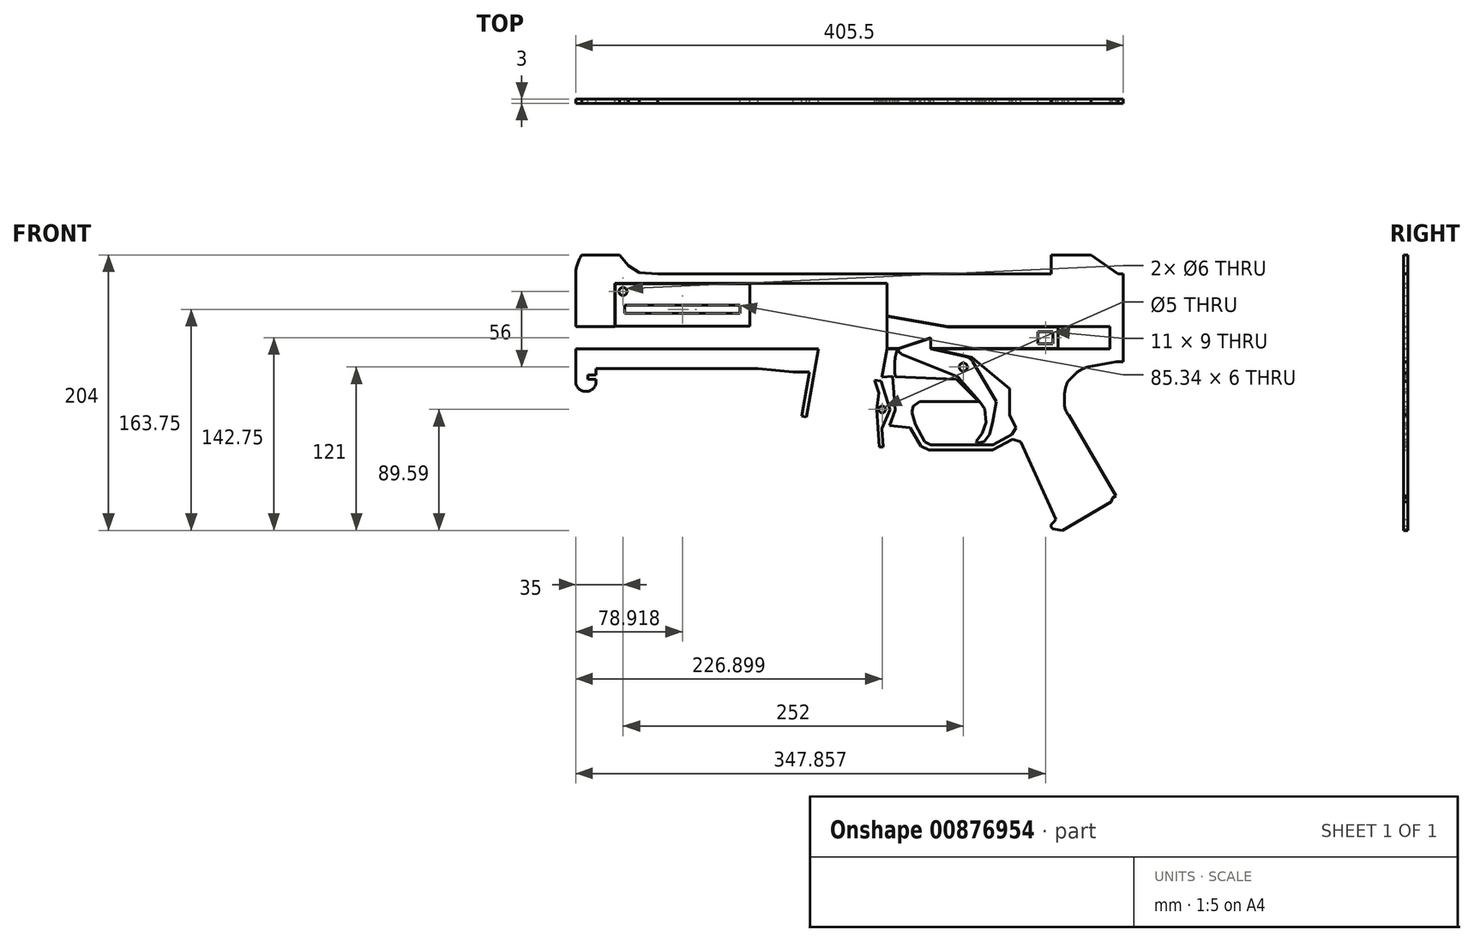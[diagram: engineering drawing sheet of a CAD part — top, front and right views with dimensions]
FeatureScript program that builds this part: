
annotation { "Feature Type Name" : "Feature", "Feature Type Description" : "" }
export const myFeature = defineFeature(function(context is Context, id is Id, definition is map)
    precondition{}
    {
        {
            var Q0;
            Q0=qCreatedBy(makeId("Front.planeOp"),FACE);
            var sketch = newSketch(context, id + "F0", { "sketchPlane" : qUnion([Q0])});
            skLineSegment(sketch, "E0", {"start": v(53.5, -65) * mm, "end": v(53.5, 0) * mm});
            skLineSegment(sketch, "E1", {"start": v(0, 0) * mm, "end": v(0, 14) * mm});
            skLineSegment(sketch, "E2", {"start": v(0, 14) * mm, "end": v(29.55, 14) * mm});
            skPoint(sketch, "E3.visualSharp", {"position": v(0, 14) * mm});
            skPoint(sketch, "E4.visualSharp", {"position": v(29.55, 14) * mm});
            skPoint(sketch, "E5.visualSharp", {"position": v(53.5, 0) * mm});
            skPoint(sketch, "E6.visualSharp", {"position": v(0, 0) * mm});
            skLineSegment(sketch, "E7", {"start": v(53.5, -65) * mm, "end": v(48.5, -65) * mm});
            skLineSegment(sketch, "E8", {"start": v(48.5, -65) * mm, "end": v(27.5, -69) * mm});
            skLineSegment(sketch, "E9", {"start": v(18.5, -73.5) * mm, "end": v(12.5, -79.5) * mm});
            skLineSegment(sketch, "E10", {"start": v(10, -90.5) * mm, "end": v(10, -96.5) * mm});
            skLineSegment(sketch, "E11", {"start": v(13, -104.5) * mm, "end": v(48, -164.5) * mm});
            skLineSegment(sketch, "E12", {"start": v(48, -164.5) * mm, "end": v(45.5, -166) * mm});
            skLineSegment(sketch, "E13", {"start": v(45.5, -166) * mm, "end": v(44.5, -169) * mm});
            skLineSegment(sketch, "E14", {"start": v(44.5, -169) * mm, "end": v(8.5, -190) * mm});
            skLineSegment(sketch, "E15", {"start": v(8.5, -190) * mm, "end": v(1.5, -189) * mm});
            skLineSegment(sketch, "E16", {"start": v(1.5, -189) * mm, "end": v(-0.5, -186.5) * mm});
            skLineSegment(sketch, "E17", {"start": v(-0.5, -186.5) * mm, "end": v(3.5, -182) * mm});
            skLineSegment(sketch, "E18", {"start": v(3.5, -182) * mm, "end": v(-22.5, -124.5) * mm});
            skLineSegment(sketch, "E19", {"start": v(-22.5, -124.5) * mm, "end": v(-28.5, -122.5) * mm});
            skLineSegment(sketch, "E20", {"start": v(-28.5, -122.5) * mm, "end": v(-43.5, -130.5) * mm});
            skLineSegment(sketch, "E21", {"start": v(-43.5, -130.5) * mm, "end": v(-90.5, -130.5) * mm});
            skLineSegment(sketch, "E22", {"start": v(-90.5, -130.5) * mm, "end": v(-96.5, -127.5) * mm});
            skLineSegment(sketch, "E23", {"start": v(-96.5, -127.5) * mm, "end": v(-104.5, -114) * mm});
            skLineSegment(sketch, "E24", {"start": v(-104.5, -114) * mm, "end": v(-131.43, -111) * mm, "construction": true});
            skArc(sketch, "E25", {"start": v(10, -90.5) * mm, "mid": v(10.63, -84.86) * mm, "end": v(12.5, -79.5) * mm});
            skArc(sketch, "E26", {"start": v(27.5, -69) * mm, "mid": v(22.69, -70.63) * mm, "end": v(18.5, -73.5) * mm});
            skArc(sketch, "E27", {"start": v(10, -96.5) * mm, "mid": v(10.77, -100.77) * mm, "end": v(13, -104.5) * mm});
            skLineSegment(sketch, "E28", {"start": v(0, 0) * mm, "end": v(-291.5, 0) * mm});
            skLineSegment(sketch, "E29", {"start": v(-291.5, 0) * mm, "end": v(-305, 1) * mm});
            skLineSegment(sketch, "E30", {"start": v(-319.5, 14) * mm, "end": v(-347.5, 14) * mm});
            skLineSegment(sketch, "E31", {"start": v(-345, -87) * mm, "end": v(-344, -87) * mm});
            skLineSegment(sketch, "E32", {"start": v(-337, -70) * mm, "end": v(-217, -70) * mm});
            skLineSegment(sketch, "E33", {"start": v(-217, -70) * mm, "end": v(-191, -72.5) * mm});
            skLineSegment(sketch, "E34", {"start": v(-191, -72.5) * mm, "end": v(-179, -72.5) * mm});
            skLineSegment(sketch, "E35", {"start": v(-179, -72.5) * mm, "end": v(-184.82, -105.5) * mm});
            skArc(sketch, "E36", {"start": v(-352, 0) * mm, "mid": v(-350.85, 7.35) * mm, "end": v(-347.5, 14) * mm});
            skLineSegment(sketch, "E37", {"start": v(-305, 1) * mm, "end": v(-313, 6) * mm});
            skLineSegment(sketch, "E38", {"start": v(-313, 6) * mm, "end": v(-319.5, 14) * mm});
            skLineSegment(sketch, "E39.bottom", {"start": v(-323, -7) * mm, "end": v(-209, -7) * mm});
            skLineSegment(sketch, "E39.left", {"start": v(-323, -7) * mm, "end": v(-323, -39) * mm});
            skLineSegment(sketch, "E40", {"start": v(-352, -80) * mm, "end": v(-352, -55.5) * mm});
            skLineSegment(sketch, "E41", {"start": v(-352, 0) * mm, "end": v(-352, -39) * mm});
            skLineSegment(sketch, "E42", {"start": v(-352, -39) * mm, "end": v(-323, -39) * mm});
            skLineSegment(sketch, "E43", {"start": v(-30.75, -104.75) * mm, "end": v(-26, -114) * mm});
            skLineSegment(sketch, "E44", {"start": v(-26, -114) * mm, "end": v(-29, -119) * mm});
            skLineSegment(sketch, "E45", {"start": v(-29, -119) * mm, "end": v(-43, -126.5) * mm});
            skLineSegment(sketch, "E46", {"start": v(-43, -126.5) * mm, "end": v(-89, -126.5) * mm});
            skLineSegment(sketch, "E47", {"start": v(-89, -126.5) * mm, "end": v(-93.5, -124.5) * mm});
            skLineSegment(sketch, "E48", {"start": v(-93.5, -124.5) * mm, "end": v(-100.5, -111.5) * mm});
            skLineSegment(sketch, "E49", {"start": v(-100.5, -111.5) * mm, "end": v(-103, -102.5) * mm});
            skLineSegment(sketch, "E50", {"start": v(-103, -102.5) * mm, "end": v(-102, -98) * mm});
            skLineSegment(sketch, "E51", {"start": v(-102, -98) * mm, "end": v(-97.5, -94.5) * mm});
            skLineSegment(sketch, "E52", {"start": v(-55.5, -124) * mm, "end": v(-55, -125) * mm});
            skLineSegment(sketch, "E53", {"start": v(-55, -125) * mm, "end": v(-52.5, -125) * mm});
            skLineSegment(sketch, "E54", {"start": v(-52.5, -125) * mm, "end": v(-49.5, -124) * mm});
            skLineSegment(sketch, "E55", {"start": v(-49.5, -124) * mm, "end": v(-45.5, -119) * mm});
            skLineSegment(sketch, "E56", {"start": v(-45.5, -119) * mm, "end": v(-43.5, -110.5) * mm});
            skLineSegment(sketch, "E57", {"start": v(-55.5, -124) * mm, "end": v(-51, -118) * mm});
            skLineSegment(sketch, "E58", {"start": v(-51, -118) * mm, "end": v(-48, -110) * mm});
            skLineSegment(sketch, "E59", {"start": v(-48, -110) * mm, "end": v(-49, -100) * mm});
            skLineSegment(sketch, "E60", {"start": v(-49, -100) * mm, "end": v(-53, -94.5) * mm});
            skLineSegment(sketch, "E61", {"start": v(-181.32, -106) * mm, "end": v(-184.82, -105.5) * mm});
            skLineSegment(sketch, "E62", {"start": v(-181.32, -106) * mm, "end": v(-172.41, -55.5) * mm});
            skLineSegment(sketch, "E63", {"start": v(-172.41, -55.5) * mm, "end": v(-352, -55.5) * mm});
            skLineSegment(sketch, "E64", {"start": v(-131.43, -111) * mm, "end": v(-121.64, -55.5) * mm, "construction": true});
            skLineSegment(sketch, "E65", {"start": v(43.5, -55.5) * mm, "end": v(43.5, -39) * mm});
            skLineSegment(sketch, "E66", {"start": v(43.5, -39) * mm, "end": v(-76.5, -39) * mm});
            skLineSegment(sketch, "E67", {"start": v(-121.64, -55.25) * mm, "end": v(-121.64, -31.25) * mm});
            skLineSegment(sketch, "E68", {"start": v(-76.5, -39) * mm, "end": v(-121.64, -31) * mm});
            skPoint(sketch, "E69", {"position": v(-317, -13) * mm});
            skPoint(sketch, "E70", {"position": v(-215, -13) * mm});
            skLineSegment(sketch, "E71", {"start": v(5.36, -55.25) * mm, "end": v(5.36, -39.25) * mm});
            skLineSegment(sketch, "E72", {"start": v(5.36, -39.25) * mm, "end": v(-76.5, -39.25) * mm});
            skLineSegment(sketch, "E73", {"start": v(-76.5, -39.25) * mm, "end": v(-121.64, -31.25) * mm});
            skLineSegment(sketch, "E74.bottom", {"start": v(-322.75, -7.25) * mm, "end": v(-223.16, -7.25) * mm});
            skLineSegment(sketch, "E74.top", {"start": v(-322.75, -38.75) * mm, "end": v(-223.16, -38.75) * mm});
            skLineSegment(sketch, "E74.left", {"start": v(-322.75, -7.25) * mm, "end": v(-322.75, -38.75) * mm});
            skLineSegment(sketch, "E74.right", {"start": v(-223.16, -7.25) * mm, "end": v(-223.16, -38.75) * mm});
            skLineSegment(sketch, "E75", {"start": v(-209, -7) * mm, "end": v(-121.64, -7) * mm});
            skLineSegment(sketch, "E76", {"start": v(-121.64, -7) * mm, "end": v(-121.64, -31) * mm});
            skPoint(sketch, "E77", {"position": v(-65, -69) * mm});
            skLineSegment(sketch, "E78", {"start": v(-40.5, -94.5) * mm, "end": v(-58.13, -64.9) * mm});
            skLineSegment(sketch, "E79", {"start": v(5.36, -55.25) * mm, "end": v(-89, -55.25) * mm});
            skLineSegment(sketch, "E80", {"start": v(-89.25, -55.5) * mm, "end": v(-63.29, -61.19) * mm});
            skLineSegment(sketch, "E81", {"start": v(-121.64, -55.25) * mm, "end": v(-113, -55.25) * mm});
            skLineSegment(sketch, "E82", {"start": v(-89, -55.25) * mm, "end": v(-89, -47.25) * mm});
            skLineSegment(sketch, "E83", {"start": v(-89, -47.25) * mm, "end": v(-113, -55.25) * mm});
            skLineSegment(sketch, "E84", {"start": v(-89.25, -55.5) * mm, "end": v(-89.25, -47.5) * mm});
            skLineSegment(sketch, "E85", {"start": v(-89.25, -47.5) * mm, "end": v(-113.25, -55.5) * mm});
            skPoint(sketch, "E86", {"position": v(-110.25, -59.5) * mm});
            skLineSegment(sketch, "E87", {"start": v(-110.25, -59.5) * mm, "end": v(-69, -76) * mm});
            skArc(sketch, "E88", {"start": v(-110.25, -59.5) * mm, "mid": v(-112.31, -57.92) * mm, "end": v(-113.25, -55.5) * mm});
            skLineSegment(sketch, "E89", {"start": v(-97.5, -94.5) * mm, "end": v(-53.5, -94.5) * mm});
            skLineSegment(sketch, "E90", {"start": v(-70, -78) * mm, "end": v(-115.3, -76.3) * mm});
            skLineSegment(sketch, "E91", {"start": v(-53, -94.5) * mm, "end": v(-69, -76) * mm});
            skLineSegment(sketch, "E92", {"start": v(-53.5, -94.5) * mm, "end": v(-70, -78) * mm});
            skLineSegment(sketch, "E93", {"start": v(-121.64, -55.5) * mm, "end": v(-114, -55.5) * mm});
            skArc(sketch, "E94", {"start": v(-114, -55.5) * mm, "mid": v(-115.73, -65.83) * mm, "end": v(-115.3, -76.3) * mm});
            skLineSegment(sketch, "E95", {"start": v(-43.5, -110.5) * mm, "end": v(-40.5, -94.5) * mm});
            skLineSegment(sketch, "E96", {"start": v(43.5, -55.5) * mm, "end": v(-87, -55.5) * mm});
            skLineSegment(sketch, "E97", {"start": v(-87, -55.5) * mm, "end": v(-58.5, -61.74) * mm});
            skLineSegment(sketch, "E98", {"start": v(-58.5, -61.74) * mm, "end": v(-30.75, -84.92) * mm});
            skPoint(sketch, "E99.visualSharp", {"position": v(-352, -87) * mm});
            skArc(sketch, "E99.filletArc", {"start": v(-352, -80) * mm, "mid": v(-349.95, -84.95) * mm, "end": v(-345, -87) * mm});
            skPoint(sketch, "E100.visualSharp", {"position": v(-337, -87) * mm});
            skArc(sketch, "E100.filletArc", {"start": v(-344, -87) * mm, "mid": v(-339.05, -84.95) * mm, "end": v(-337, -80) * mm});
            skCircle(sketch, "E101", {"center": v(-317, -13) * mm, "radius": 3 * mm});
            skPoint(sketch, "E102", {"position": v(-323, -7) * mm});
            skLineSegment(sketch, "E103", {"start": v(-104.5, -114) * mm, "end": v(-119.5, -112.33) * mm});
            skLineSegment(sketch, "E104", {"start": v(-125.2, -114.45) * mm, "end": v(-124.32, -128.13) * mm});
            skLineSegment(sketch, "E105", {"start": v(-124.32, -128.13) * mm, "end": v(-127.32, -128.33) * mm});
            skLineSegment(sketch, "E106", {"start": v(-127.32, -128.33) * mm, "end": v(-129.1, -100.38) * mm});
            skLineSegment(sketch, "E107", {"start": v(-129.1, -100.38) * mm, "end": v(-127.43, -88.32) * mm});
            skLineSegment(sketch, "E108", {"start": v(-127.43, -88.32) * mm, "end": v(-130.8, -78.59) * mm});
            skLineSegment(sketch, "E109", {"start": v(-130.8, -78.59) * mm, "end": v(-125.87, -79.45) * mm});
            skLineSegment(sketch, "E110", {"start": v(-125.87, -79.45) * mm, "end": v(-119.2, -100.45) * mm});
            skLineSegment(sketch, "E111", {"start": v(-119.2, -100.45) * mm, "end": v(-125.2, -114.45) * mm});
            skLineSegment(sketch, "E112", {"start": v(-129.1, -100.38) * mm, "end": v(-119.2, -100.45) * mm, "construction": true});
            skCircle(sketch, "E113", {"center": v(-125.1, -100.4) * mm, "radius": 2.5 * mm});
            skLineSegment(sketch, "E114", {"start": v(-119.5, -112.33) * mm, "end": v(-115.5, -100.83) * mm});
            skLineSegment(sketch, "E115", {"start": v(-115.5, -100.83) * mm, "end": v(-117.5, -75.83) * mm});
            skLineSegment(sketch, "E116", {"start": v(-117.5, -75.83) * mm, "end": v(-125.35, -76.5) * mm});
            skCircle(sketch, "E117", {"center": v(-65, -69) * mm, "radius": 3 * mm});
            skArc(sketch, "E118", {"start": v(-63.29, -61.19) * mm, "mid": v(-60.32, -62.51) * mm, "end": v(-58.13, -64.9) * mm});
            skPoint(sketch, "E119", {"position": v(-69, -76) * mm});
            skLineSegment(sketch, "E120", {"start": v(-121.64, -55.5) * mm, "end": v(-125.35, -76.5) * mm});
            skLineSegment(sketch, "E121", {"start": v(-30.75, -104.75) * mm, "end": v(-30.75, -84.92) * mm});
            skLineSegment(sketch, "E122", {"start": v(1.36, -42.75) * mm, "end": v(1.36, -51.75) * mm});
            skPoint(sketch, "E123", {"position": v(1.36, -47.25) * mm});
            skPoint(sketch, "E124", {"position": v(5.36, -47.25) * mm});
            skLineSegment(sketch, "E125", {"start": v(1.36, -42.75) * mm, "end": v(-9.64, -42.75) * mm});
            skLineSegment(sketch, "E126", {"start": v(-9.64, -42.75) * mm, "end": v(-9.64, -51.75) * mm});
            skLineSegment(sketch, "E127", {"start": v(-9.64, -51.75) * mm, "end": v(1.36, -51.75) * mm});
            skPoint(sketch, "E128", {"position": v(-316, -23) * mm});
            skLineSegment(sketch, "E129.bottom", {"start": v(-315.75, -23.25) * mm, "end": v(-230.41, -23.25) * mm});
            skLineSegment(sketch, "E129.top", {"start": v(-315.75, -29.25) * mm, "end": v(-230.41, -29.25) * mm});
            skLineSegment(sketch, "E129.left", {"start": v(-315.75, -23.25) * mm, "end": v(-315.75, -29.25) * mm});
            skLineSegment(sketch, "E129.right", {"start": v(-230.41, -23.25) * mm, "end": v(-230.41, -29.25) * mm});
            skLineSegment(sketch, "E130", {"start": v(29.55, 14) * mm, "end": v(49.5, 0) * mm});
            skLineSegment(sketch, "E131", {"start": v(49.5, 0) * mm, "end": v(53.5, 0) * mm});
            skLineSegment(sketch, "E132", {"start": v(-337, -70) * mm, "end": v(-337, -75) * mm});
            skLineSegment(sketch, "E133", {"start": v(-337, -75) * mm, "end": v(-343, -75) * mm});
            skLineSegment(sketch, "E134", {"start": v(-343, -75) * mm, "end": v(-343, -78) * mm});
            skLineSegment(sketch, "E135", {"start": v(-343, -78) * mm, "end": v(-337, -78) * mm});
            skLineSegment(sketch, "E136", {"start": v(-337, -78) * mm, "end": v(-337, -80) * mm});
            skSolve(sketch);
        }
        {
            var Q0;
            Q0 = qSketchRegion(id + "F0", true);
            extrude(context, id + "F1", {"entities" : qUnion([Q0]), "depth" : 3 * mm, "offsetDistance" : 25 * mm});
        }
    });
